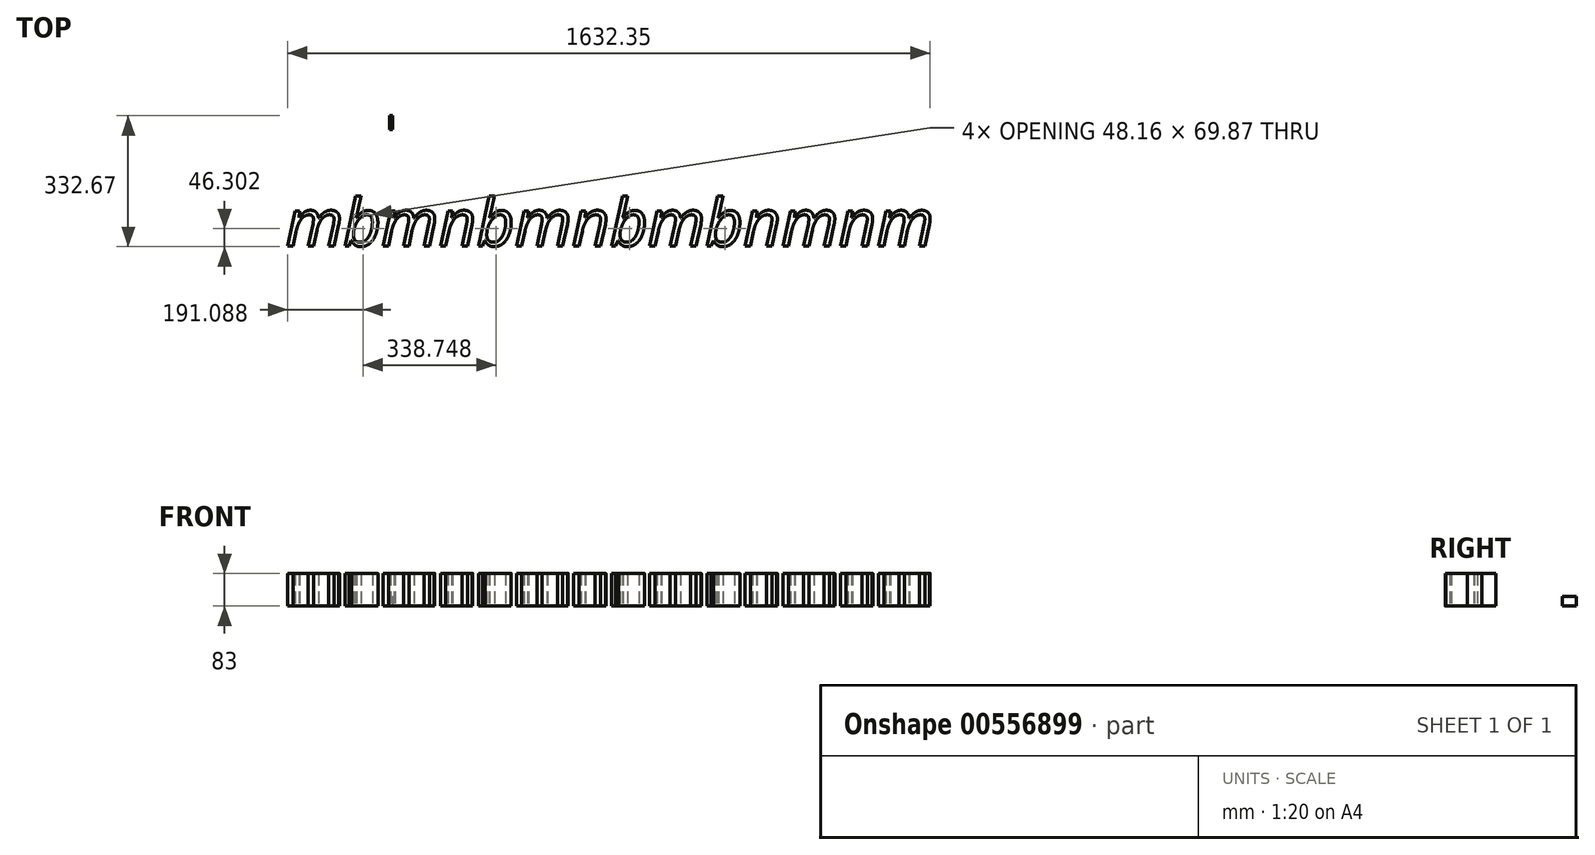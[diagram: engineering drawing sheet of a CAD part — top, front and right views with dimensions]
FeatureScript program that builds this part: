
annotation { "Feature Type Name" : "Feature", "Feature Type Description" : "" }
export const myFeature = defineFeature(function(context is Context, id is Id, definition is map)
    precondition{}
    {
        {
            var Q0;
            Q0=qCreatedBy(makeId("Top.planeOp"),FACE);
            var sketch = newSketch(context, id + "F0", { "sketchPlane" : qUnion([Q0])});
            skText(sketch, "E0", { "text": "mbmnbmnbmbnmnm", "fontName": "OpenSans-Italic.ttf"});
            const initialGuessF0  = {"E0": [-0.16996, -0.11112, 1, 0, 0.12036]};
            skSetInitialGuess(sketch, initialGuessF0);
            skSolve(sketch);
        }
        {
            var Q0;
            Q0 = qSketchRegion(id + "F0", true);
            var Q1;
            Q1 = qConstructionFilter(qBodyType(qCreatedBy(id + "F0" ,EDGE), BodyType.WIRE), ConstructionObject.NO);
            extrude(context, id + "F1", {"entities" : qUnion([Q0]), "surfaceEntities" : qUnion([Q1]), "depth" : 83 * mm, "offsetDistance" : 25 * mm});
        }
        {
            var Q0;
            Q0=qCreatedBy(makeId("Top.planeOp"),FACE);
            var sketch = newSketch(context, id + "F2", { "sketchPlane" : qUnion([Q0])});
            skLineSegment(sketch, "E1.bottom", {"start": v(93.95, 219.9) * mm, "end": v(101.1, 219.9) * mm});
            skLineSegment(sketch, "E1.top", {"start": v(93.95, 184.45) * mm, "end": v(101.1, 184.45) * mm});
            skLineSegment(sketch, "E1.left", {"start": v(93.95, 219.9) * mm, "end": v(93.95, 184.45) * mm});
            skLineSegment(sketch, "E1.right", {"start": v(101.1, 219.9) * mm, "end": v(101.1, 184.45) * mm});
            skSolve(sketch);
        }
        {
            var Q0;
            Q0 = qSketchRegion(id + "F2", true);
            extrude(context, id + "F3", {"entities" : qUnion([Q0]), "depth" : 25 * mm, "offsetDistance" : 25 * mm});
        }
    });
